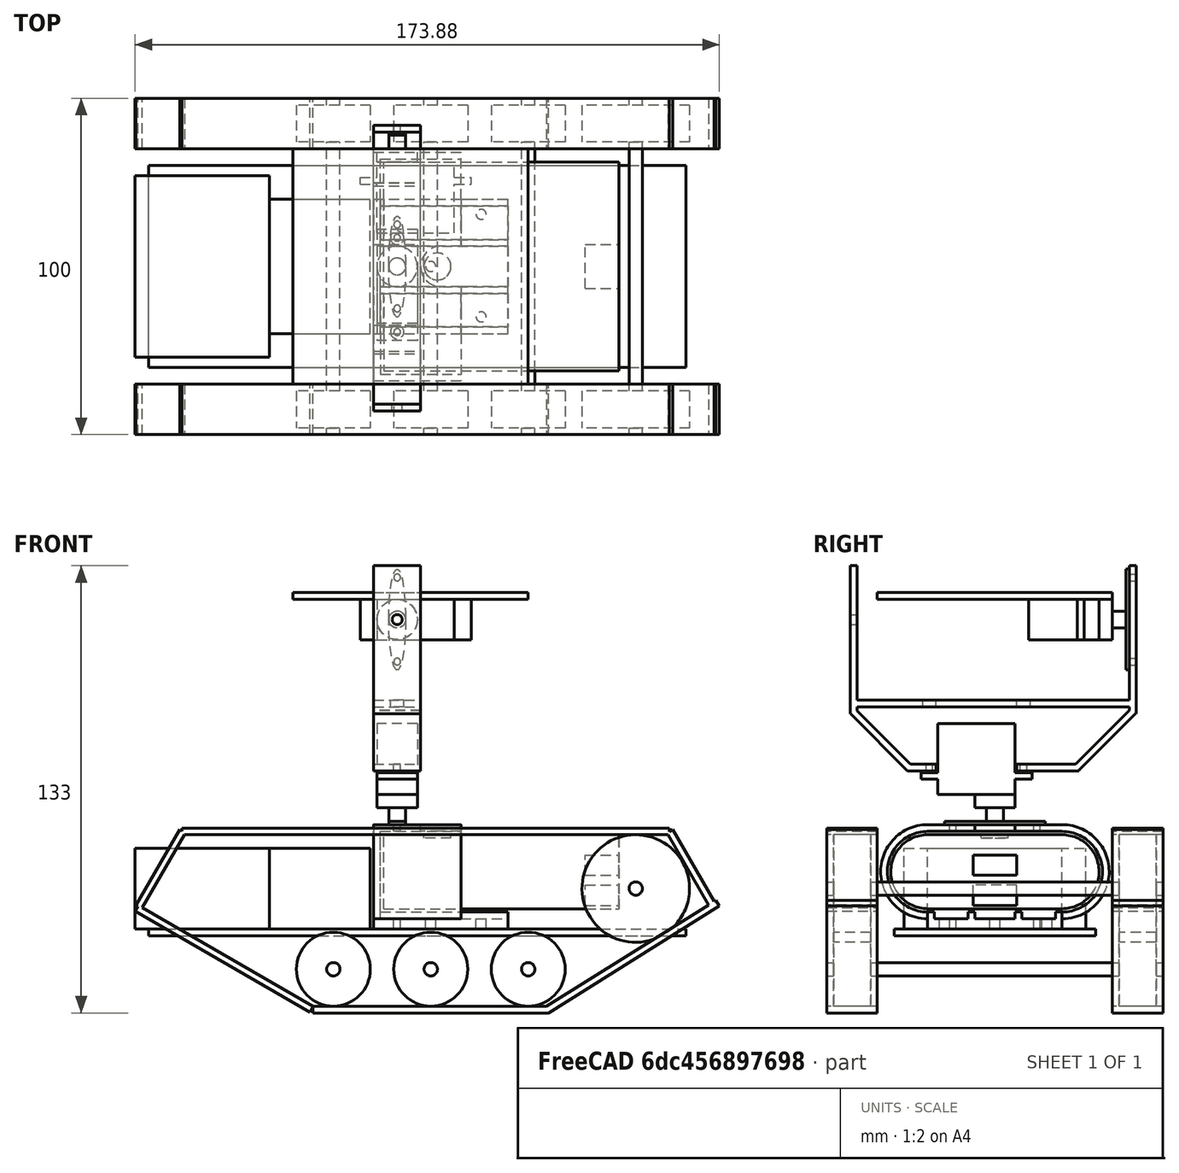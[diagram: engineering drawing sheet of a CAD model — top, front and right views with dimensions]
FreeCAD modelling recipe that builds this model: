
FCSTD DOCUMENT
Label: androidtank_3
License: CC-BY 3.0
LicenseURL: http://creativecommons.org/licenses/by/3.0/
objects: Part::Box×32, Part::Cylinder×32, Part::MultiFuse×19, Part::Cut×4, Part::FeaturePython×2, App::DocumentObjectGroup×1
note: 89 computed .brp shape members not serialized (recipe doc carries the construction recipe); baked Part::Feature solids carry a one-line shape summary decoded from their .brp

FEATURE [Part::Box] Box  label="MainFrame"
  Height = 2
  Length = 160
  Width = 60
FEATURE [Part::Box] Box001001  label="Moter Unit2"
  Height = 24
  Length = 30
  Placement = pos=(36,10,2) rot=(0,0,1;0rad)
  Width = 40
FEATURE [Part::Cylinder] Cylinder002  label="Wheel1"
  Angle = 360
  Height = 11
  Placement = pos=(20,-7,14) rot=(1,0,0;1.5708rad)
  Radius = 16
FEATURE [Part::Cylinder] Cylinder  label="Shaft"
  Angle = 360
  Height = 100
  Placement = pos=(20,-20,14) rot=(-1,0,0;1.5708rad)
  Radius = 2
FEATURE [Part::Cylinder] Cylinder002001  label="Wheel2"
  Angle = 360
  Height = 11
  Placement = pos=(20,78,14) rot=(1,0,0;1.5708rad)
  Radius = 16
FEATURE [Part::MultiFuse] Fusion001  label="WheelSet2"
  Placement = pos=(125,0,0) rot=(0,0,1;0rad)
  Shapes = -> [Cylinder,Cylinder002,Cylinder002001]
FEATURE [Part::Box] Box001002
  Height = 2
  Length = 145
  Placement = pos=(10,-20,30) rot=(0,0,1;0rad)
  Width = 15
FEATURE [Part::Box] Box001002001
  Height = 2
  Length = 70
  Placement = pos=(49,-20,-23) rot=(0,0,1;0rad)
  Width = 15
FEATURE [Part::Box] Box001002001001
  Height = 2
  Length = 60
  Placement = pos=(119,-20,-23) rot=(0,-1,0;0.558505rad)
  Width = 15
FEATURE [Part::Box] Box001002001002
  Height = 2
  Length = 60
  Placement = pos=(49,-20,-21) rot=(0,1,0;3.66519rad)
  Width = 15
FEATURE [Part::Box] Box001002001003
  Height = 2
  Length = 26
  Placement = pos=(-2,-20,8) rot=(0,-1,0;1.0472rad)
  Width = 15
FEATURE [Part::Box] Box001002001003001
  Height = 2
  Length = 26
  Placement = pos=(169,-20,9) rot=(0,-1,0;2.0944rad)
  Width = 15
FEATURE [Part::MultiFuse] Fusion002001002  label="Caterpiller1"
  Shapes = -> [Box001002,Box001002001,Box001002001002,Box001002001001,Box001002001003,Box001002001003001]
FEATURE [Part::MultiFuse] Fusion002001002001  label="Caterpiller2"
  Placement = pos=(0,85,0) rot=(0,0,1;0rad)
  Shapes = -> [Box001002,Box001002001,Box001002001002,Box001002001001,Box001002001003,Box001002001003001]
FEATURE [Part::Cylinder] Cylinder002001001002  label="Wheel006"
  Angle = 360
  Height = 11
  Placement = pos=(20,78,14) rot=(1,0,0;1.5708rad)
  Radius = 11
FEATURE [Part::Cylinder] Cylinder002001001002001  label="Wheel007"
  Angle = 360
  Height = 11
  Placement = pos=(20,-7,14) rot=(1,0,0;1.5708rad)
  Radius = 11
FEATURE [Part::Cylinder] Cylinder002001002001  label="Shaft002"
  Angle = 360
  Height = 100
  Placement = pos=(20,-20,14) rot=(-1,0,0;1.5708rad)
  Radius = 2
FEATURE [Part::MultiFuse] Fusion002001002002002  label="SWheelSet1"
  Placement = pos=(35,0,-24) rot=(0,0,1;0rad)
  Shapes = -> [Cylinder002001002001,Cylinder002001001002,Cylinder002001001002001]
FEATURE [Part::MultiFuse] Fusion002001002002002001  label="SWheelSet2"
  Placement = pos=(64,0,-24) rot=(0,0,1;0rad)
  Shapes = -> [Cylinder002001002001,Cylinder002001001002,Cylinder002001001002001]
FEATURE [Part::MultiFuse] Fusion002001002002002001001  label="SWheelSet3"
  Placement = pos=(93,0,-24) rot=(0,0,1;0rad)
  Shapes = -> [Cylinder002001002001,Cylinder002001001002,Cylinder002001001002001]
FEATURE [Part::Box] Box001002001003002
  Height = 22
  Length = 70
  Placement = pos=(0,0,-11) rot=(0,0,1;0rad)
  Width = 40
FEATURE [Part::Cylinder] Cylinder002001001002002
  Angle = 360
  Height = 70
  Placement = pos=(0,0,0) rot=(0,1,0;1.5708rad)
  Radius = 11
FEATURE [Part::Cylinder] Cylinder001
  Angle = 360
  Height = 70
  Placement = pos=(0,40,0) rot=(0,1,0;1.5708rad)
  Radius = 11
FEATURE [Part::Cylinder] Cylinder002001001002003  label="PowerButton"
  Angle = 360
  Height = 2
  Placement = pos=(16,20,10) rot=(0,0,1;0rad)
  Radius = 4
FEATURE [Part::Box] Box001002001003003  label="USB1"
  Height = 6
  Length = 15
  Placement = pos=(60,13.5,-1) rot=(0,0,1;0rad)
  Width = 13
FEATURE [Part::Box] Box001001001  label="USB2"
  Height = 6
  Length = 15
  Placement = pos=(60,13.5,-10) rot=(0,0,1;0rad)
  Width = 13
FEATURE [Part::MultiFuse] Fusion002001002002002001002
  Shapes = -> [Cylinder001,Box001002001003002,Cylinder002001001002002]
FEATURE [Part::MultiFuse] Fusion001001
  Shapes = -> [Box001001001,Cylinder002001001002003,Box001002001003003]
FEATURE [Part::Cut] Cut  label="Eneloop"
  Base = -> Fusion002001002002002001002
  Placement = pos=(70,10,19) rot=(0,0,1;0rad)
  Tool = -> Fusion001001
FEATURE [Part::Cylinder] Cylinder001001  label="Cylinder002"
  Angle = 360
  Height = 26
  Placement = pos=(0,50,19) rot=(0,1,0;1.5708rad)
  Radius = 14
FEATURE [Part::Box] Box001002001003002001  label="Box002"
  Height = 28
  Length = 26
  Placement = pos=(0,10,5) rot=(0,0,1;0rad)
  Width = 40
FEATURE [Part::Cylinder] Cylinder002001001002002001  label="Cylinder003"
  Angle = 360
  Height = 26
  Placement = pos=(0,10,19) rot=(0,1,0;1.5708rad)
  Radius = 14
FEATURE [Part::Box] Box001  label="Moter Unit1"
  Height = 24
  Length = 40
  Placement = pos=(-4,3,2) rot=(0,0,1;0rad)
  Width = 54
FEATURE [App::DocumentObjectGroup] ____________  label="DriveFrame"
  Group = -> [Box,Box001,Box001001,Fusion002001002,Fusion002001002001,Fusion002001002002002,Fusion002001002002002001,Fusion002001002002002001001,Fusion001]
FEATURE [Part::Box] Box001002001003002001001  label="Box003"
  Height = 5
  Length = 40
  Placement = pos=(0,10,2) rot=(0,0,1;0rad)
  Width = 40
FEATURE [Part::Box] Box001002001003002001002  label="Box004"
  Height = 24
  Length = 26
  Placement = pos=(2,10,7) rot=(0,0,1;0rad)
  Width = 40
FEATURE [Part::Cylinder] Cylinder001001001  label="Cylinder004"
  Angle = 360
  Height = 26
  Placement = pos=(2,50,19) rot=(0,1,0;1.5708rad)
  Radius = 12
FEATURE [Part::Cylinder] Cylinder002001001002002001001  label="Cylinder005"
  Angle = 360
  Height = 26
  Placement = pos=(2,10,19) rot=(0,1,0;1.5708rad)
  Radius = 12
FEATURE [Part::Cylinder] Cylinder002001001002003001  label="PowerButton001"
  Angle = 360
  Height = 4
  Placement = pos=(20,30,30) rot=(0,0,1;0rad)
  Radius = 6
FEATURE [Part::Box] Box001002001003002001003  label="Box005"
  Height = 4
  Length = 10
  Placement = pos=(20,24,30) rot=(0,0,1;0rad)
  Width = 12
FEATURE [Part::Box] Box001002001003002001001001  label="Box006"
  Height = 3
  Length = 40
  Placement = pos=(2,12,5) rot=(0,0,1;0rad)
  Width = 10
FEATURE [Part::Box] Box001002001003002001001001001  label="Box007"
  Height = 3
  Length = 40
  Placement = pos=(2,24,5) rot=(0,0,1;0rad)
  Width = 12
FEATURE [Part::Box] Box001002001003002001001001001001  label="Box008"
  Height = 3
  Length = 40
  Placement = pos=(2,38,5) rot=(0,0,1;0rad)
  Width = 10
FEATURE [Part::MultiFuse] Fusion002001002002002001003
  Shapes = -> [Box001002001003002001,Cylinder001001,Cylinder002001001002002001,Box001002001003002001001]
FEATURE [Part::MultiFuse] Fusion002001002002002001004
  Shapes = -> [Box001002001003002001002,Cylinder002001001002002001001,Cylinder001001001,Box001002001003002001001001001001,Box001002001003002001001001001,Box001002001003002001001001,Box001002001003002001003,Cylinder002001001002003001]
FEATURE [Part::Cut] Cut001  label="BatteryFrame"
  Base = -> Fusion002001002002002001003
  Placement = pos=(67,0,0) rot=(0,0,1;0rad)
  Tool = -> Fusion002001002002002001004
FEATURE [Part::Cylinder] Cylinder002001001002002001002001  label="Cylinder007"
  Angle = 360
  Height = 40
  Placement = pos=(74,17.5,0) rot=(0,0,1;0rad)
  Radius = 1
FEATURE [Part::Cylinder] Cylinder002001001002002001002  label="Cylinder006"
  Angle = 360
  Height = 40
  Placement = pos=(74,42.5,0) rot=(0,0,1;0rad)
  Radius = 1
FEATURE [Part::Cylinder] Cylinder002001001002002001002001001  label="Cylinder008"
  Angle = 360
  Height = 40
  Placement = pos=(84,30,0) rot=(0,0,1;0rad)
  Radius = 1.5
FEATURE [Part::Cylinder] Cylinder002001001002002001002001002  label="Cylinder009"
  Angle = 360
  Height = 40
  Placement = pos=(99,45.5,0) rot=(0,0,1;0rad)
  Radius = 1.5
FEATURE [Part::Cylinder] Cylinder002001001002002001002001003  label="Cylinder0010"
  Angle = 360
  Height = 40
  Placement = pos=(99,15,0) rot=(0,0,1;0rad)
  Radius = 1.5
FEATURE [Part::MultiFuse] Fusion002001002002002001005  label="BatteryFrameHoles"
  Shapes = -> [Cylinder002001001002002001002001,Cylinder002001001002002001002,Cylinder002001001002002001002001003,Cylinder002001001002002001002001002,Cylinder002001001002002001002001001]
FEATURE [Part::Cut] Cut002  label="BatteryFrame2"
  Base = -> Cut001
  Tool = -> Fusion002001002002002001005
FEATURE [Part::Box] Box001002001003002001001001001002  label="ServoBody"
  Height = 21
  Length = 23
  Width = 12
FEATURE [Part::Cylinder] Cylinder002001001002002001002001004  label="ServoBody2"
  Angle = 360
  Height = 4
  Placement = pos=(6,6,21) rot=(0,0,1;0rad)
  Radius = 6
FEATURE [Part::Box] Box001002001003002001001001001003  label="ServoBody3"
  Height = 2
  Length = 33
  Placement = pos=(-5,0,14.5) rot=(0,0,1;0rad)
  Width = 12
FEATURE [Part::Cylinder] Cylinder001001002  label="ServoAxis"
  Angle = 360
  Height = 4
  Placement = pos=(6,6,24) rot=(0,0,1;0rad)
  Radius = 2.5
FEATURE [Part::MultiFuse] Fusion005  label="ServoArmL"
  Shapes = -> [Cylinder001001002,Box001002001003002001001001001003,Box001002001003002001001001001002,Cylinder002001001002002001002001004]
FEATURE [Part::Cylinder] Cylinder002001001002002001002001005
  Angle = 360
  Height = 2
  Radius = 2.5
FEATURE [Part::FeaturePython] Scale  # Draft clone (typed FeaturePython)
  Objects = -> [Cylinder002001001002002001002001005]
  Placement = pos=(0,0,1) rot=(0,0,1;0rad)
  Scale = (6,1,0.5)
FEATURE [Part::MultiFuse] Fusion  label="Arm"
  Placement = pos=(6,6,28) rot=(0,0,1;0rad)
  Shapes = -> [Cylinder002001001002002001002001005,Scale]
FEATURE [Part::MultiFuse] Fusion006  label="ServoYaw"
  Placement = pos=(80,36,63) rot=(0.707107,-0.707107,0;3.14159rad)
  Shapes = -> [Fusion005,Fusion]
FEATURE [Part::Box] Box001002001003002001001001001004  label="ServoBody004"
  Height = 21
  Length = 23
  Width = 12
FEATURE [Part::Cylinder] Cylinder002001001002002001002001006  label="ServoBody005"
  Angle = 360
  Height = 4
  Placement = pos=(6,6,21) rot=(0,0,1;0rad)
  Radius = 6
FEATURE [Part::Box] Box001002001003002001001001001005  label="ServoBody006"
  Height = 2
  Length = 33
  Placement = pos=(-5,0,14.5) rot=(0,0,1;0rad)
  Width = 12
FEATURE [Part::Cylinder] Cylinder001001003  label="ServoAxis001"
  Angle = 360
  Height = 4
  Placement = pos=(6,6,24) rot=(0,0,1;0rad)
  Radius = 2.5
FEATURE [Part::MultiFuse] Fusion005001  label="ServoArmL001"
  Shapes = -> [Cylinder001001003,Box001002001003002001001001001005,Box001002001003002001001001001004,Cylinder002001001002002001002001006]
FEATURE [Part::Cylinder] Cylinder002001001002002001002001007
  Angle = 360
  Height = 2
  Radius = 2.5
FEATURE [Part::FeaturePython] Scale001  # Draft clone (typed FeaturePython)
  Objects = -> [Cylinder002001001002002001002001007]
  Placement = pos=(0,0,1) rot=(0,0,1;0rad)
  Scale = (6,1,0.5)
FEATURE [Part::MultiFuse] Fusion002001002002002001006  label="Arm001"
  Placement = pos=(6,6,28) rot=(0,0,1;1.5708rad)
  Shapes = -> [Cylinder002001001002002001002001007,Scale001]
FEATURE [Part::MultiFuse] Fusion006001  label="ServoPitch"
  Placement = pos=(68,40,100) rot=(-1,0,0;1.57079rad)
  Shapes = -> [Fusion005001,Fusion002001002002002001006]
FEATURE [Part::Box] Box001002001003002001001001001006  label="Box009"
  Height = 2
  Length = 70
  Placement = pos=(43,-5,100) rot=(0,0,1;0rad)
  Width = 70
FEATURE [Part::Box] Box001002001003002001001001001006001  label="Box010"
  Height = 44
  Length = 14
  Placement = pos=(67,70,66) rot=(0,0,1;0rad)
  Width = 2
FEATURE [Part::Box] Box001002001003002001001001001006001001  label="Box011"
  Height = 2
  Length = 13
  Placement = pos=(67.5,12.5,48) rot=(0,0,1;0rad)
  Width = 23.5
FEATURE [Part::Box] Box001002001003002001001001001006001001001  label="Box012"
  Height = 44
  Length = 14
  Placement = pos=(67,-13,66) rot=(0,0,1;0rad)
  Width = 2
FEATURE [Part::Cylinder] Cylinder002001001002002001002001008  label="Hole1"
  Angle = 360
  Height = 20
  Placement = pos=(74,-20,94) rot=(-1,0,0;1.5708rad)
  Radius = 1.5
FEATURE [Part::Cylinder] Cylinder002001001002002001002001008001  label="Hole2"
  Angle = 360
  Height = 20
  Placement = pos=(74,60,106.5) rot=(-1,0,0;1.5708rad)
  Radius = 1
FEATURE [Part::Cylinder] Cylinder002001001002002001002001008001001  label="Hole4"
  Angle = 360
  Height = 20
  Placement = pos=(74,38.5,41) rot=(0,0,1;0rad)
  Radius = 1
FEATURE [Part::Cylinder] Cylinder002001001002002001002001008001001001  label="Hole3"
  Angle = 360
  Height = 20
  Placement = pos=(74,60,81.5) rot=(-1,0,0;1.5708rad)
  Radius = 1
FEATURE [Part::Cylinder] Cylinder002001001002002001002001008001001002  label="Hole5"
  Angle = 360
  Height = 20
  Placement = pos=(74,10.5,41) rot=(0,0,1;0rad)
  Radius = 1
FEATURE [Part::Box] Box001002001003002001001001001006001001001001  label="Box013"
  Height = 24
  Length = 14
  Placement = pos=(67,4,49) rot=(1,0,0;0.785397rad)
  Width = 2
FEATURE [Part::Box] Box001002001003002001001001001006001001001001001  label="Box014"
  Height = 24
  Length = 14
  Placement = pos=(67,53.41,50.41) rot=(-1,0,0;0.785397rad)
  Width = 2
FEATURE [Part::Box] Box001002001003002001001001001006001001002001  label="Box016"
  Height = 2
  Length = 14
  Placement = pos=(67,4,49) rot=(0,0,1;0rad)
  Width = 8.5
FEATURE [Part::Box] Box001002001003002001001001001006001001002001001  label="Box017"
  Height = 2
  Length = 14
  Placement = pos=(67,36.5,49) rot=(0,0,1;0rad)
  Width = 18.5
FEATURE [Part::Box] Box001002001003002001001001001006001001002001002  label="Box015"
  Height = 2
  Length = 14
  Placement = pos=(67,-13,68) rot=(0,0,1;0rad)
  Width = 85
FEATURE [Part::MultiFuse] Fusion002001002002002001009
  Shapes = -> [Box001002001003002001001001001006001,Box001002001003002001001001001006001001001001,Box001002001003002001001001001006001001001,Box001002001003002001001001001006001001001001001,Box001002001003002001001001001006001001002001,Box001002001003002001001001001006001001002001002,Box001002001003002001001001001006001001002001001]
FEATURE [Part::Cylinder] Cylinder002001001002002001002001008001001002001  label="Hole006"
  Angle = 360
  Height = 20
  Placement = pos=(74,10.5,60) rot=(0,0,1;0rad)
  Radius = 2
FEATURE [Part::Cylinder] Cylinder002001001002002001002001008001001002002  label="Hole007"
  Angle = 360
  Height = 20
  Placement = pos=(74,38.5,60) rot=(0,0,1;0rad)
  Radius = 2
FEATURE [Part::MultiFuse] Fusion002001002002002001010
  Shapes = -> [Cylinder002001001002002001002001008001,Box001002001003002001001001001006001001,Cylinder002001001002002001002001008001001,Cylinder002001001002002001002001008,Cylinder002001001002002001002001008001001001,Cylinder002001001002002001002001008001001002,Cylinder002001001002002001002001008001001002002,Cylinder002001001002002001002001008001001002001]
FEATURE [Part::Cut] Cut003
  Base = -> Fusion002001002002002001009
  Tool = -> Fusion002001002002002001010
